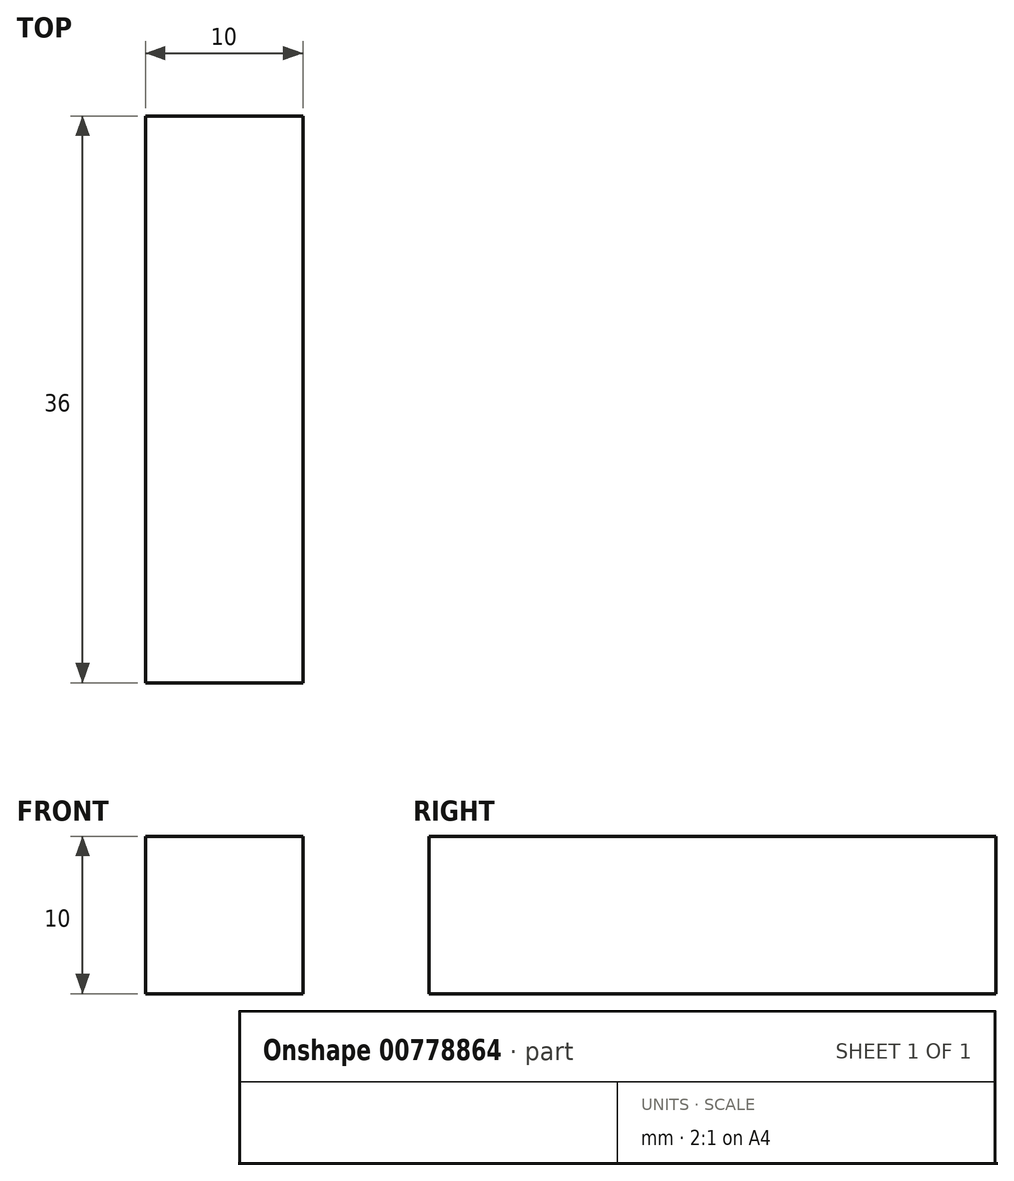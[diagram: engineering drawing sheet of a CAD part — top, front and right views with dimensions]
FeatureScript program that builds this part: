
annotation { "Feature Type Name" : "Feature", "Feature Type Description" : "" }
export const myFeature = defineFeature(function(context is Context, id is Id, definition is map)
    precondition{}
    {
        {
            var Q0;
            Q0=qCreatedBy(makeId("Top.planeOp"),FACE);
            var sketch = newSketch(context, id + "F0", { "sketchPlane" : qUnion([Q0])});
            skLineSegment(sketch, "E0.bottom", {"start": v(-10, 0) * mm, "end": v(0, 0) * mm});
            skLineSegment(sketch, "E0.top", {"start": v(-10, -36) * mm, "end": v(0, -36) * mm});
            skLineSegment(sketch, "E0.left", {"start": v(-10, 0) * mm, "end": v(-10, -36) * mm});
            skLineSegment(sketch, "E0.right", {"start": v(0, 0) * mm, "end": v(0, -36) * mm});
            skSolve(sketch);
        }
        {
            var Q0;
            Q0=makeQuery(id+"F0.imprint","IMPRINT",FACE,{"disambiguationData":[TD([[makeQuery(id+"F0.imprint","IMPRINT",EDGE,{"derivedFrom":sQuery(id+"F0.wireOp",EDGE,"E0.bottom")}),-1.0]])]});
            extrude(context, id + "F1", {"entities" : qUnion([Q0]), "depth" : 10 * mm, "offsetDistance" : 25 * mm});
        }
    });
